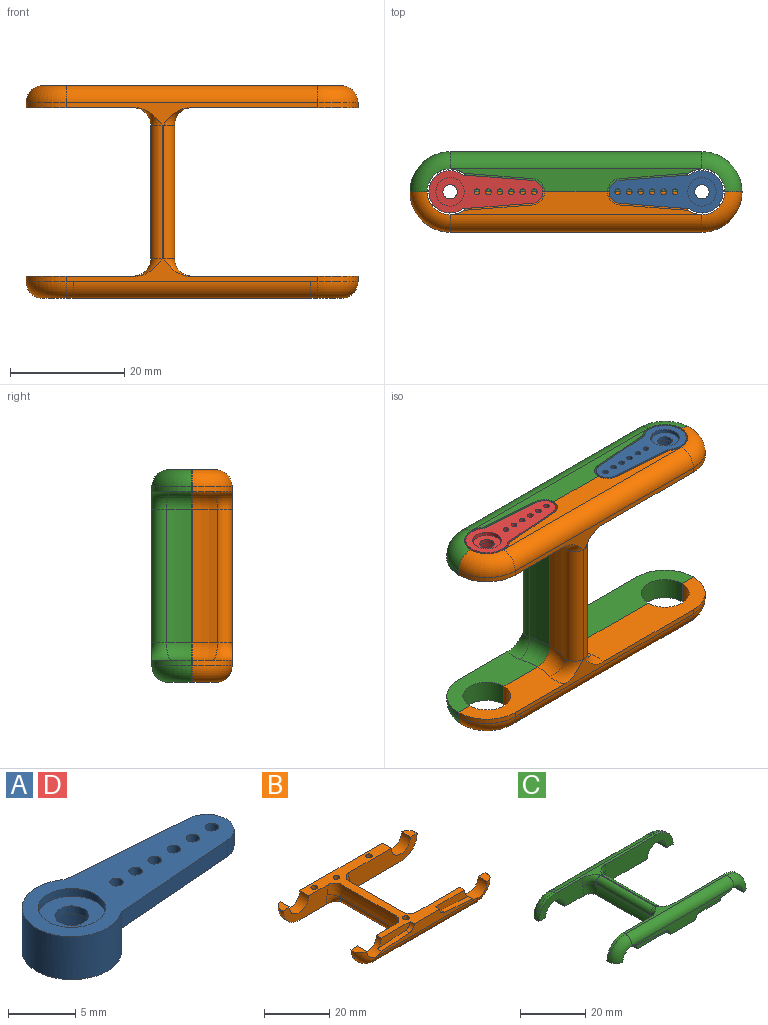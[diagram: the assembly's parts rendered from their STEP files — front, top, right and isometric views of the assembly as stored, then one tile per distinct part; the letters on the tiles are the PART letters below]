
ASSEMBLY  parts=4 mates=3
PART A: 18 faces, bbox 19.9x7.4x3.9 mm
  f0: cylinder r=1.25mm len=2.5mm, axis (0,0,1), area 5.5mm2, adj f1,f7
  f1: plane 5x5mm, normal (0,0,1), area 14.7mm2, adj f0,f2
  f2: cylinder r=2.5mm len=5mm, axis (0,0,1), area 11mm2, adj f1,f3
  f3: plane 19.9x7.4mm, normal (0,0,1), area 78.2mm2, adj f2,f4,f8,f9,f10,f11,f12,f13
  f4: cylinder r=3.7mm len=7.4mm, axis (0,0,1), area 80.4mm2, adj f3,f5,f8,f9,f17
  f5: plane 7.4x7.4mm, normal (0,0,-1), area 24.9mm2, adj f4,f6
  f6: cylinder r=2.4mm len=4.8mm, axis (0,0,1), area 37.7mm2, adj f5,f7
  f7: plane 4.8x4.8mm, normal (0,0,-1), area 13.2mm2, adj f0,f6
  f8: plane 12.12x1.5mm, normal (0.08,1,0), area 18.2mm2, adj f3,f4,f16,f17
  f9: plane 12.12x1.5mm, normal (0.08,-1,0), area 18.2mm2, adj f3,f4,f16,f17
  f10: cylinder r=0.5mm len=1.5mm, axis (0,0,-1), area 4.7mm2, adj f3,f17
  f11: cylinder r=0.5mm len=1.5mm, axis (0,0,-1), area 4.7mm2, adj f3,f17
  f12: cylinder r=0.5mm len=1.5mm, axis (0,0,-1), area 4.7mm2, adj f3,f17
  f13: cylinder r=0.5mm len=1.5mm, axis (0,0,-1), area 4.7mm2, adj f3,f17
  f14: cylinder r=0.5mm len=1.5mm, axis (0,0,-1), area 4.7mm2, adj f3,f17
  f15: cylinder r=0.5mm len=1.5mm, axis (0,0,-1), area 4.7mm2, adj f3,f17
  f16: cylinder r=2mm len=3.99mm, axis (0,0,-1), area 9mm2, adj f3,f8,f9,f17
  f17: plane 13.97x5.9mm, normal (0,0,-1), area 54.8mm2, adj f4,f8,f9,f10,f11,f12,f13,f14
PART B: 55 faces, bbox 59.2x37.4x12.7 mm
  f0: plane 3.9x3mm, normal (0,0,1), area 9.8mm2, adj f31,f35,f36,f40
  f1: cylinder r=3mm len=41.44mm, axis (1,0,0), area 195.3mm2, adj f3,f12,f13,f33
  f2: cylinder r=2mm len=23.4mm, axis (0,1,0), area 82.1mm2, adj f3,f10,f11,f22
  f3: plane 44x31.21mm, normal (0,0,-1), area 102.9mm2, adj f1,f2,f4,f7,f8,f9,f10,f11
  f4: cylinder r=2mm len=23.4mm, axis (0,1,0), area 87.1mm2, adj f3,f8,f9,f29
  f5: plane 12.04x1.8mm, normal (0.08,0,1), area 21.7mm2, adj f37,f38,f39,f41
  f6: plane 12.04x1.8mm, normal (-0.08,0,1), area 21.7mm2, adj f14,f15,f40,f41
  f7: cylinder r=3mm len=44mm, axis (-1,0,0), area 207.3mm2, adj f3,f16,f35,f41
  f8: torus R=5mm, axis (0,-1,0), area 15.2mm2, adj f3,f4,f28,f31
  f9: torus R=5mm, axis (0,-1,0), area 15.2mm2, adj f3,f4,f27,f30
  f10: torus R=5mm, axis (0,-1,0), area 13.6mm2, adj f2,f3,f17,f23
  f11: torus R=5mm, axis (0,-1,0), area 13.6mm2, adj f2,f3,f18,f21
  f12: bspline ~3.17x3.17mm, area 5.9mm2, adj f1,f3,f19,f20
  f13: bspline ~3.17x3.17mm, area 5.9mm2, adj f1,f3,f25,f26
  f14: cylinder r=2.3mm len=2.29mm, axis (0,-1,0), area 6.2mm2, adj f6,f15,f41,f44
  f15: plane 14.16x3.24mm, normal (0,-1,0), area 33.3mm2, adj f6,f14,f40,f44
  f16: torus R=4mm, axis (0,1,0), area 43.7mm2, adj f7,f34,f39,f45
  f17: torus R=22.5mm, axis (0,-1,0), area 21mm2, adj f10,f22,f23,f44
  f18: torus R=22.5mm, axis (0,-1,0), area 21mm2, adj f11,f21,f22,f44
  f19: torus R=4mm, axis (0,1,0), area 42.5mm2, adj f12,f20,f24,f43
  f20: cylinder r=4.2mm len=8.4mm, axis (0,1,0), area 51.5mm2, adj f12,f19,f21,f33,f43,f44
  f21: plane 29.5x7mm, normal (0,-1,0), area 166.7mm2, adj f3,f11,f18,f20,f24,f43,f44
  f22: cylinder r=25.5mm len=23.4mm, axis (0,1,0), area 109.1mm2, adj f2,f17,f18,f44
  f23: plane 29.5x7mm, normal (0,1,0), area 169.3mm2, adj f3,f10,f17,f34,f39,f44,f45
  f24: cylinder r=7mm len=7mm, axis (0,-1,0), area 10mm2, adj f3,f19,f21,f43
  f25: torus R=4mm, axis (0,1,0), area 42.5mm2, adj f13,f26,f32,f42
  f26: cylinder r=4.2mm len=8.4mm, axis (0,1,0), area 51.5mm2, adj f13,f25,f30,f33,f42,f44
  f27: torus R=12.5mm, axis (0,-1,0), area 19.7mm2, adj f9,f29,f30,f44
  f28: torus R=12.5mm, axis (0,-1,0), area 19.7mm2, adj f8,f29,f31,f44
  f29: cylinder r=15.5mm len=23.4mm, axis (0,1,0), area 105.1mm2, adj f4,f27,f28,f44
  f30: plane 19.5x7mm, normal (0,-1,0), area 95.5mm2, adj f3,f9,f26,f27,f32,f42,f44
  f31: plane 19.5x7mm, normal (0,1,0), area 98.1mm2, adj f0,f3,f8,f28,f36,f40,f44
  f32: cylinder r=7mm len=7mm, axis (0,-1,0), area 10mm2, adj f3,f25,f30,f42
  f33: plane 41.44x4mm, normal (0,1,0), area 148.6mm2, adj f1,f20,f26,f44
  f34: cylinder r=7mm len=7mm, axis (0,-1,0), area 9.9mm2, adj f3,f16,f23,f45
  f35: torus R=4mm, axis (0,1,0), area 43.7mm2, adj f0,f7,f36,f40
  f36: cylinder r=7mm len=7mm, axis (0,-1,0), area 9.9mm2, adj f0,f3,f31,f35
  f37: cylinder r=2.3mm len=2.29mm, axis (0,-1,0), area 6.2mm2, adj f5,f38,f41,f44
  f38: plane 14.16x3.24mm, normal (0,-1,0), area 33.3mm2, adj f5,f37,f39,f44
  f39: cylinder r=4mm len=8mm, axis (0,-1,0), area 42.2mm2, adj f5,f16,f23,f38,f41,f44,f45
  f40: cylinder r=4mm len=8mm, axis (0,-1,0), area 42.2mm2, adj f0,f6,f15,f31,f35,f41,f44
  f41: plane 44x4mm, normal (0,-1,0), area 84.3mm2, adj f5,f6,f7,f14,f37,f39,f40,f44
  f42: plane 3.9x2.8mm, normal (0,0,1), area 9mm2, adj f25,f26,f30,f32
  f43: plane 3.9x2.8mm, normal (0,0,1), area 9mm2, adj f19,f20,f21,f24
  f44: plane 37.2x36mm, normal (0,0,1), area 317.6mm2, adj f14,f15,f17,f18,f20,f21,f22,f23
  f45: plane 3.9x3mm, normal (0,0,1), area 9.8mm2, adj f16,f23,f34,f39
  f46: cylinder r=3mm len=2mm, axis (1,0,0), area 3.4mm2, adj f47
  f47: cylinder r=1mm len=5.31mm, axis (0,0,1), area 32.1mm2, adj f44,f46
  f48: cylinder r=3mm len=2mm, axis (1,0,0), area 1.7mm2, adj f49,f50
  f49: plane 2x0.97mm, normal (0,0,1), area 1.5mm2, adj f48,f50
  f50: cylinder r=1mm len=5.5mm, axis (0,0,1), area 34.3mm2, adj f44,f48,f49
  f51: cylinder r=3mm len=2mm, axis (1,0,0), area 3.4mm2, adj f52
  f52: cylinder r=1mm len=5.31mm, axis (0,0,1), area 32.1mm2, adj f44,f51
  f53: plane 2x2mm, normal (0,0,1), area 3.1mm2, adj f54
  f54: cylinder r=1mm len=5.5mm, axis (0,0,1), area 34.6mm2, adj f44,f53
PART C: 55 faces, bbox 59.2x37.4x12.7 mm
  f0: plane 44x4mm, normal (0,-1,0), area 84.3mm2, adj f1,f2,f18,f19,f21,f22,f26,f43
  f1: cylinder r=4mm len=8mm, axis (0,-1,0), area 42.2mm2, adj f0,f12,f20,f22,f25,f43,f45
  f2: cylinder r=4mm len=8mm, axis (0,-1,0), area 42.2mm2, adj f0,f9,f17,f18,f27,f43,f44
  f3: cylinder r=7mm len=7mm, axis (0,-1,0), area 9.9mm2, adj f5,f12,f25,f45
  f4: cylinder r=7mm len=7mm, axis (0,-1,0), area 9.9mm2, adj f5,f9,f27,f44
  f5: plane 44x31.21mm, normal (0,0,1), area 102.9mm2, adj f3,f4,f7,f8,f9,f11,f12,f13
  f6: plane 41.44x4mm, normal (0,1,0), area 148.6mm2, adj f15,f16,f38,f43
  f7: cylinder r=7mm len=7mm, axis (0,-1,0), area 10mm2, adj f5,f13,f40,f41
  f8: cylinder r=7mm len=7mm, axis (0,-1,0), area 10mm2, adj f5,f11,f36,f42
  f9: plane 29.5x7mm, normal (0,1,0), area 169.3mm2, adj f2,f4,f5,f32,f33,f43,f44
  f10: cylinder r=25.5mm len=23.4mm, axis (0,1,0), area 109.1mm2, adj f23,f32,f34,f43
  f11: plane 29.5x7mm, normal (0,-1,0), area 166.7mm2, adj f5,f8,f16,f34,f35,f42,f43
  f12: plane 19.5x7mm, normal (0,1,0), area 98.1mm2, adj f1,f3,f5,f28,f29,f43,f45
  f13: plane 19.5x7mm, normal (0,-1,0), area 95.5mm2, adj f5,f7,f15,f30,f31,f41,f43
  f14: cylinder r=15.5mm len=23.4mm, axis (0,1,0), area 105.1mm2, adj f24,f29,f31,f43
  f15: cylinder r=4.2mm len=8.4mm, axis (0,1,0), area 51.5mm2, adj f6,f13,f39,f40,f41,f43
  f16: cylinder r=4.2mm len=8.4mm, axis (0,1,0), area 51.5mm2, adj f6,f11,f36,f37,f42,f43
  f17: plane 14.16x3.24mm, normal (0,-1,0), area 33.3mm2, adj f2,f18,f19,f43
  f18: plane 12.04x1.8mm, normal (0.08,0,-1), area 21.7mm2, adj f0,f2,f17,f19
  f19: cylinder r=2.3mm len=2.29mm, axis (0,-1,0), area 6.2mm2, adj f0,f17,f18,f43
  f20: plane 14.16x3.24mm, normal (0,-1,0), area 33.3mm2, adj f1,f21,f22,f43
  f21: cylinder r=2.3mm len=2.29mm, axis (0,-1,0), area 6.2mm2, adj f0,f20,f22,f43
  f22: plane 12.04x1.8mm, normal (-0.08,0,-1), area 21.7mm2, adj f0,f1,f20,f21
  f23: cylinder r=2mm len=23.4mm, axis (0,1,0), area 82.1mm2, adj f5,f10,f33,f35
  f24: cylinder r=2mm len=23.4mm, axis (0,1,0), area 87.1mm2, adj f5,f14,f28,f30
  f25: torus R=4mm, axis (0,1,0), area 43.7mm2, adj f1,f3,f26,f45
  f26: cylinder r=3mm len=44mm, axis (1,0,0), area 207.3mm2, adj f0,f5,f25,f27
  f27: torus R=4mm, axis (0,1,0), area 43.7mm2, adj f2,f4,f26,f44
  f28: torus R=5mm, axis (0,-1,0), area 15.2mm2, adj f5,f12,f24,f29
  f29: torus R=12.5mm, axis (0,-1,0), area 19.7mm2, adj f12,f14,f28,f43
  f30: torus R=5mm, axis (0,-1,0), area 15.2mm2, adj f5,f13,f24,f31
  f31: torus R=12.5mm, axis (0,-1,0), area 19.7mm2, adj f13,f14,f30,f43
  f32: torus R=22.5mm, axis (0,-1,0), area 21mm2, adj f9,f10,f33,f43
  f33: torus R=5mm, axis (0,-1,0), area 13.6mm2, adj f5,f9,f23,f32
  f34: torus R=22.5mm, axis (0,-1,0), area 21mm2, adj f10,f11,f35,f43
  f35: torus R=5mm, axis (0,-1,0), area 13.6mm2, adj f5,f11,f23,f34
  f36: torus R=4mm, axis (0,1,0), area 42.5mm2, adj f8,f16,f37,f42
  f37: bspline ~3.17x3.17mm, area 5.9mm2, adj f5,f16,f36,f38
  f38: cylinder r=3mm len=41.44mm, axis (-1,0,0), area 195.3mm2, adj f5,f6,f37,f39
  f39: bspline ~3.17x3.17mm, area 5.9mm2, adj f5,f15,f38,f40
  f40: torus R=4mm, axis (0,1,0), area 42.5mm2, adj f7,f15,f39,f41
  f41: plane 3.9x2.8mm, normal (0,0,-1), area 9mm2, adj f7,f13,f15,f40
  f42: plane 3.9x2.8mm, normal (0,0,-1), area 9mm2, adj f8,f11,f16,f36
  f43: plane 37.2x36mm, normal (0,0,-1), area 317.6mm2, adj f0,f1,f2,f6,f9,f10,f11,f12
  f44: plane 3.9x3mm, normal (0,0,-1), area 9.8mm2, adj f2,f4,f9,f27
  f45: plane 3.9x3mm, normal (0,0,-1), area 9.8mm2, adj f1,f3,f12,f25
  f46: cylinder r=1mm len=5.31mm, axis (0,0,1), area 32.2mm2, adj f43,f47
  f47: cylinder r=3mm len=2mm, axis (-1,0,0), area 3.4mm2, adj f46
  f48: cylinder r=1mm len=5.5mm, axis (0,0,1), area 34.3mm2, adj f43,f49,f50
  f49: cylinder r=3mm len=2mm, axis (-1,0,0), area 1.7mm2, adj f48,f50
  f50: plane 2x0.97mm, normal (0,0,-1), area 1.5mm2, adj f48,f49
  f51: cylinder r=1mm len=5.31mm, axis (0,0,1), area 32.2mm2, adj f43,f52
  f52: cylinder r=3mm len=2mm, axis (-1,0,0), area 3.4mm2, adj f51
  f53: cylinder r=1mm len=5.5mm, axis (0,0,1), area 34.6mm2, adj f43,f54
  f54: plane 2x2mm, normal (0,0,-1), area 3.1mm2, adj f53
PART D: same geometry as A
PLACE A rot(axis=(0,0,1),180deg) t=(39.45,37.32,2.47)mm
PLACE B rot(axis=(-1,0,0),90deg) t=(17.65,37.32,3.92)mm
PLACE C rot(axis=(-1,0,0),90deg) t=(17.65,37.32,3.92)mm
PLACE D t=(5.85,37.32,2.47)mm
MATE fastened D.f0 <-> B.f25  axis (0,0,1) through (0.65,37.32,22.47)mm
MATE fastened B.f54 <-> C.f53  axis (0,1,0) through (17.65,37.32,18.37)mm
MATE fastened A.f0 <-> B.f16  axis (0,0,1) through (44.65,37.32,22.47)mm
